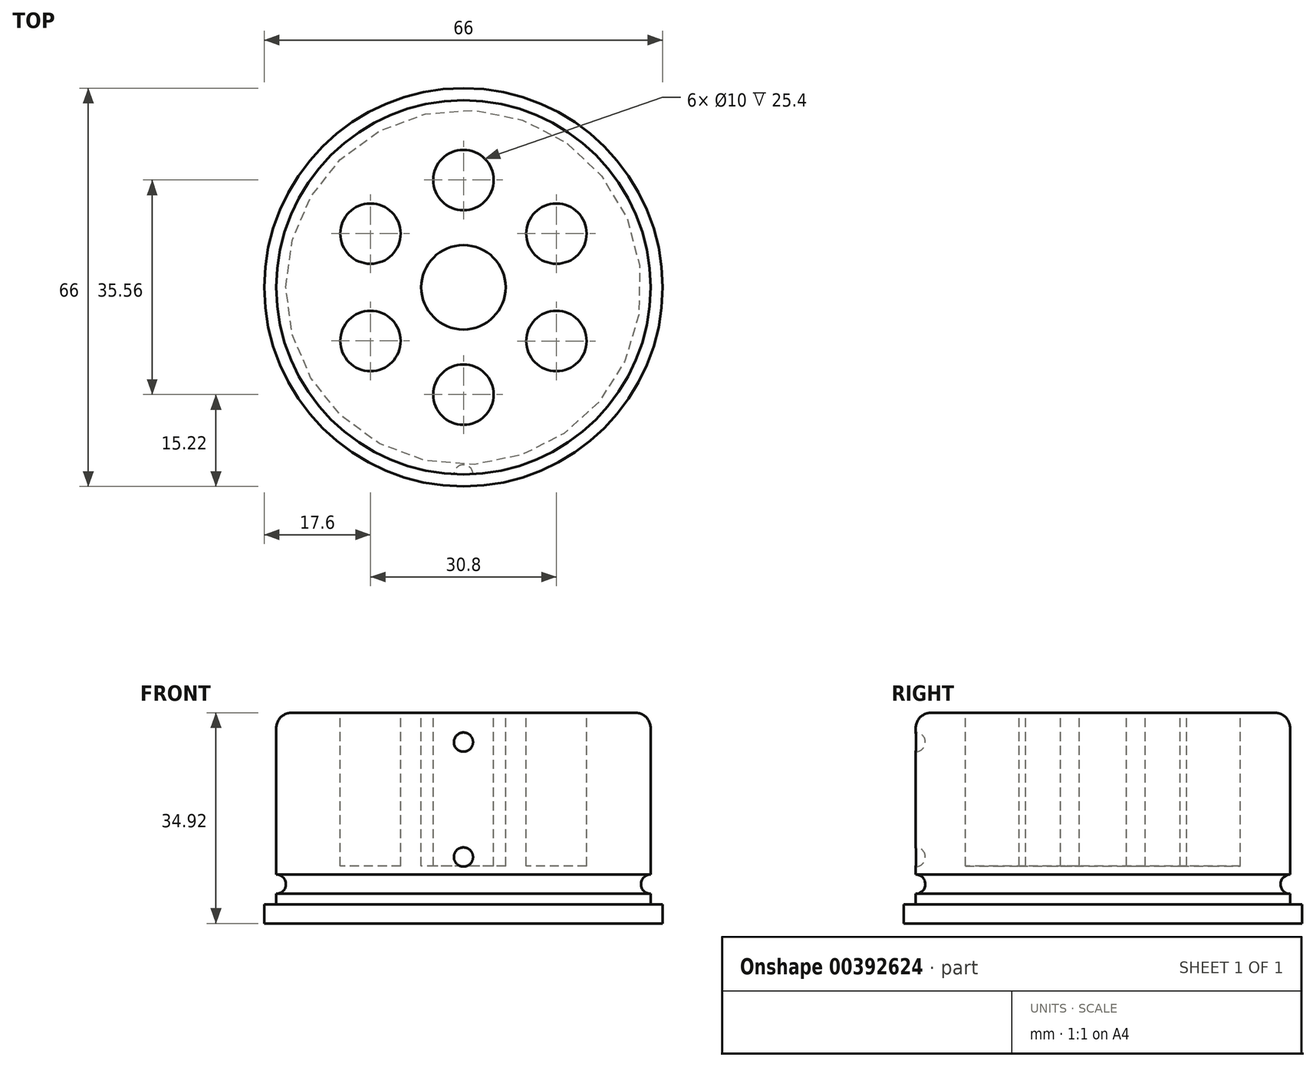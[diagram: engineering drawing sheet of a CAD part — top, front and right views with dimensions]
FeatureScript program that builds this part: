
annotation { "Feature Type Name" : "Feature", "Feature Type Description" : "" }
export const myFeature = defineFeature(function(context is Context, id is Id, definition is map)
    precondition{}
    {
        {
            var Q0;
            Q0=qCreatedBy(makeId("Top.planeOp"),FACE);
            var sketch = newSketch(context, id + "F0", { "sketchPlane" : qUnion([Q0])});
            skCircle(sketch, "E0", {"center": v(0, 0) * mm, "radius": 33 * mm});
            skSolve(sketch);
        }
        {
            var Q0;
            Q0 = qSketchRegion(id + "F0", true);
            extrude(context, id + "F1", {"entities" : qUnion([Q0]), "depth" : 3.17 * mm});
        }
        {
            var Q0;
            Q0=makeQuery(id+"F1.opExtrude","CAP_FACE",FACE,{"disambiguationData":[OSD([sQuery(id+"F0.wireOp",EDGE,"E0")])],"isStart":false});
            var sketch = newSketch(context, id + "F2", { "sketchPlane" : qUnion([Q0])});
            skCircle(sketch, "E1", {"center": v(0, 0) * mm, "radius": 31 * mm});
            skSolve(sketch);
        }
        {
            var Q0;
            Q0 = qSketchRegion(id + "F2", true);
            extrude(context, id + "F3", {"entities" : qUnion([Q0]), "operationType" : NewBodyOperationType.ADD, "depth" : 31.75 * mm});
        }
        {
            var Q0;
            Q0=qCreatedBy(makeId("Right.planeOp"),FACE);
            var sketch = newSketch(context, id + "F4", { "sketchPlane" : qUnion([Q0])});
            skCircle(sketch, "E2", {"center": v(-31, 30.05) * mm, "radius": 1.59 * mm});
            skCircle(sketch, "E3", {"center": v(-31, 11) * mm, "radius": 1.59 * mm});
            skLineSegment(sketch, "E4", {"start": v(-32.59, 30) * mm, "end": v(-32.59, 11) * mm});
            skLineSegment(sketch, "E5", {"start": v(-32.59, 11) * mm, "end": v(-32.59, 30) * mm});
            skLineSegment(sketch, "E6", {"start": v(-29.42, 30) * mm, "end": v(-29.41, 11) * mm});
            skLineSegment(sketch, "E7", {"start": v(-29.41, 11) * mm, "end": v(-29.42, 30) * mm});
            skLineSegment(sketch, "E8", {"start": v(0, 0) * mm, "end": v(-31, 0) * mm});
            skLineSegment(sketch, "E9", {"start": v(-31, 0) * mm, "end": v(-31, 35.03) * mm});
            skLineSegment(sketch, "E10", {"start": v(-31, 35.03) * mm, "end": v(-31, 0) * mm});
            skSolve(sketch);
        }
        {
            var Q0;
            {var subQ0=sQuery(id+"F4.wireOp",EDGE,"E2");var subQ1=makeQuery(id+"F4.imprint","INTERSECT",VERTEX,{"derivedFrom":[subQ0,sQuery(id+"F4.wireOp",EDGE,"E5")]});Q0=makeQuery(id+"F4.imprint","IMPRINT",FACE,{"disambiguationData":[TD([[makeQuery(id+"F4.imprint","IMPRINT",EDGE,{"disambiguationData":[TD([[subQ1,1.0]])],"derivedFrom":subQ0}),1.0]])]});}
            var Q1;
            {var subQ0=sQuery(id+"F4.wireOp",EDGE,"E3");var subQ1=makeQuery(id+"F4.imprint","INTERSECT",VERTEX,{"derivedFrom":[subQ0,sQuery(id+"F4.wireOp",EDGE,"E5")]});Q1=makeQuery(id+"F4.imprint","IMPRINT",FACE,{"disambiguationData":[TD([[makeQuery(id+"F4.imprint","IMPRINT",EDGE,{"disambiguationData":[TD([[subQ1,1.0]])],"derivedFrom":subQ0}),1.0]])]});}
            var Q2;
            {var subQ0=sQuery(id+"F4.wireOp",EDGE,"E5");Q2=makeQuery(id+"F4.imprint","IMPRINT",FACE,{"disambiguationData":[TD([[makeQuery(id+"F4.imprint","IMPRINT",EDGE,{"derivedFrom":subQ0}),-1.0]])]});}
            var Q3;
            Q3=sQuery(id+"F4.wireOp",EDGE,"E10");
            revolve(context, id + "F5", {"operationType" : NewBodyOperationType.REMOVE, "entities" : qUnion([Q0, Q1, Q2]), "axis" : qUnion([Q3]), "revolveType" : RevolveType.FULL, "oppositeDirection" : true});
        }
        {
            var Q0;
            Q0=qCreatedBy(makeId("Right.planeOp"),FACE);
            var sketch = newSketch(context, id + "F6", { "sketchPlane" : qUnion([Q0])});
            skCircle(sketch, "E11", {"center": v(-31, 6.5) * mm, "radius": 1.59 * mm});
            skLineSegment(sketch, "E12", {"start": v(0, 0) * mm, "end": v(-31, 0) * mm});
            skLineSegment(sketch, "E13", {"start": v(-31, 0) * mm, "end": v(-31, 34.7) * mm});
            skLineSegment(sketch, "E14", {"start": v(-31, 34.7) * mm, "end": v(-31, 0) * mm});
            skLineSegment(sketch, "E15", {"start": v(0, 0) * mm, "end": v(0, 34.85) * mm});
            skLineSegment(sketch, "E16", {"start": v(0, 34.85) * mm, "end": v(0, 0) * mm});
            skSolve(sketch);
        }
        {
            var Q0;
            Q0 = qSketchRegion(id + "F6", true);
            var Q1;
            Q1=sQuery(id+"F6.wireOp",EDGE,"E16");
            revolve(context, id + "F7", {"operationType" : NewBodyOperationType.REMOVE, "entities" : qUnion([Q0]), "axis" : qUnion([Q1]), "revolveType" : RevolveType.FULL, "oppositeDirection" : true});
        }
        {
            var Q0;
            Q0=makeQuery(id+"F3.opExtrude","CAP_EDGE",EDGE,{"disambiguationData":[OSD([sQuery(id+"F2.wireOp",EDGE,"E1")])],"isStart":false});
            fillet(context, id + "F8", {"entities" : qUnion([Q0]), "radius" : 2.54 * mm, "tangentPropagation" : true, "allowEdgeOverflow" : false});
        }
        {
            var Q0;
            Q0=makeQuery(id+"F3.opExtrude","CAP_FACE",FACE,{"disambiguationData":[OSD([sQuery(id+"F2.wireOp",EDGE,"E1")])],"isStart":false});
            var sketch = newSketch(context, id + "F9", { "sketchPlane" : qUnion([Q0])});
            skCircle(sketch, "E17", {"center": v(0, 0) * mm, "radius": 6.99 * mm});
            skCircle(sketch, "E18", {"center": v(0, 17.78) * mm, "radius": 5 * mm});
            skLineSegment(sketch, "E19", {"start": v(0, 0) * mm, "end": v(0, 17.78) * mm});
            skCircle(sketch, "E20.1.0", {"center": v(-15.4, 8.9) * mm, "radius": 5 * mm});
            skCircle(sketch, "E20.2.0", {"center": v(-15.4, -8.89) * mm, "radius": 5 * mm});
            skCircle(sketch, "E20.3.0", {"center": v(0, -17.78) * mm, "radius": 5 * mm});
            skCircle(sketch, "E20.4.0", {"center": v(15.4, -8.9) * mm, "radius": 5 * mm});
            skCircle(sketch, "E20.5.0", {"center": v(15.4, 8.9) * mm, "radius": 5 * mm});
            skSolve(sketch);
        }
        {
            var Q0;
            Q0 = qSketchRegion(id + "F9", true);
            extrude(context, id + "F10", {"entities" : qUnion([Q0]), "operationType" : NewBodyOperationType.REMOVE, "oppositeDirection" : true, "depth" : 25.4 * mm});
        }
    });
